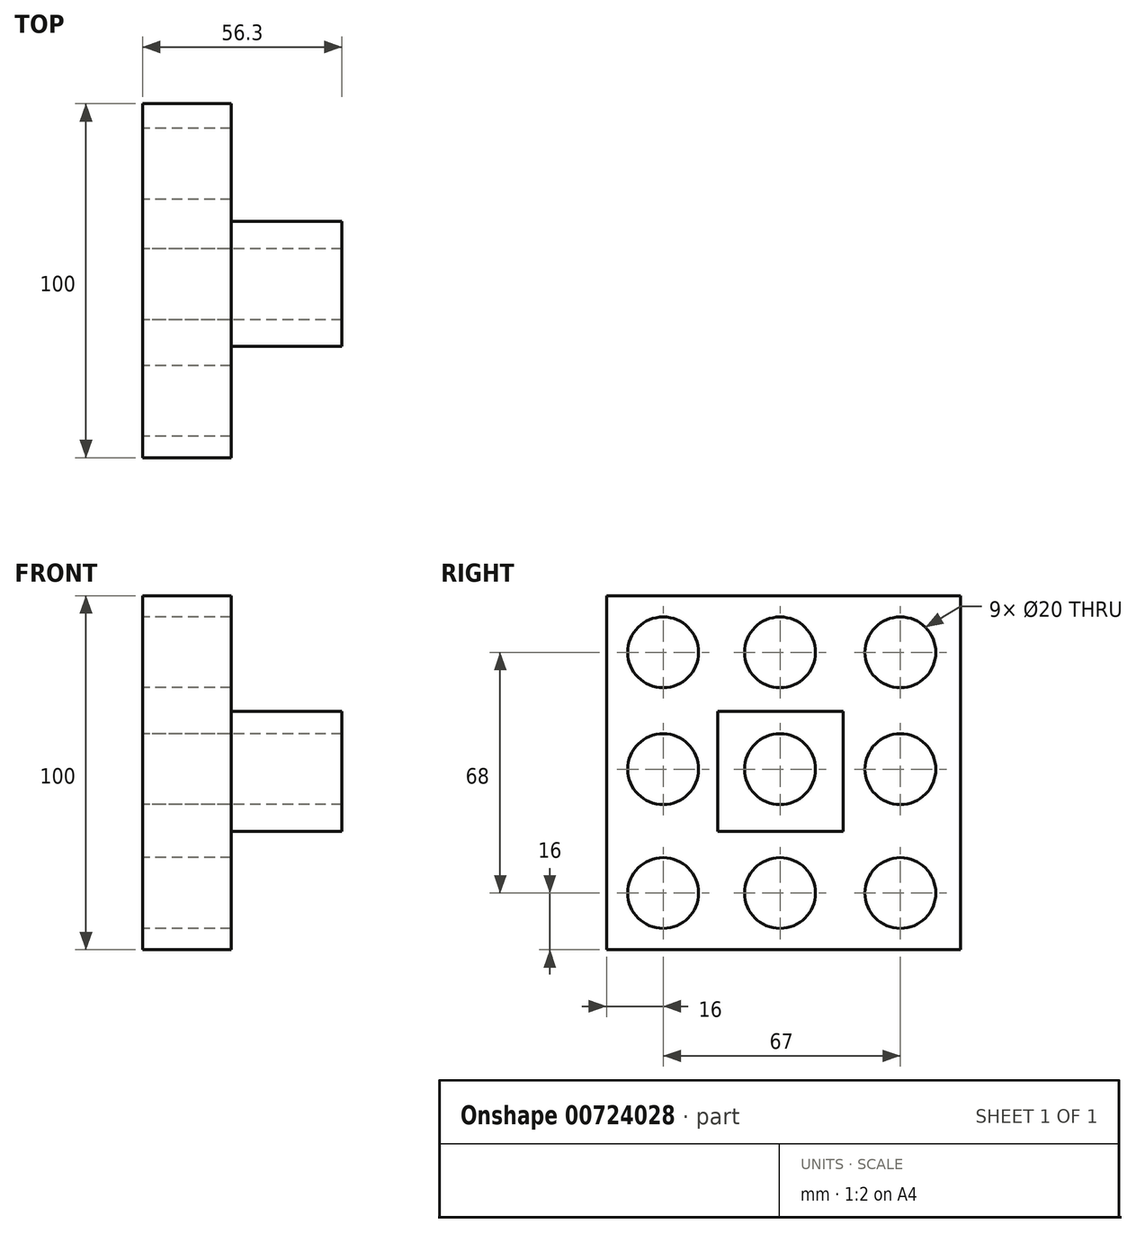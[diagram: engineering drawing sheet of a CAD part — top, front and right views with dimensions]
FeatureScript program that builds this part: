
annotation { "Feature Type Name" : "Feature", "Feature Type Description" : "" }
export const myFeature = defineFeature(function(context is Context, id is Id, definition is map)
    precondition{}
    {
        {
            var Q0;
            Q0=qCreatedBy(makeId("Right.planeOp"),FACE);
            var sketch = newSketch(context, id + "F0", { "sketchPlane" : qUnion([Q0])});
            skLineSegment(sketch, "E0.bottom", {"start": v(0, 0) * mm, "end": v(100, 0) * mm});
            skLineSegment(sketch, "E0.top", {"start": v(0, 100) * mm, "end": v(100, 100) * mm});
            skLineSegment(sketch, "E0.left", {"start": v(0, 0) * mm, "end": v(0, 100) * mm});
            skLineSegment(sketch, "E0.right", {"start": v(100, 0) * mm, "end": v(100, 100) * mm});
            skLineSegment(sketch, "E1.0", {"start": v(33, 0) * mm, "end": v(33, 100) * mm});
            skLineSegment(sketch, "E2.0", {"start": v(67, 0) * mm, "end": v(67, 100) * mm});
            skLineSegment(sketch, "E3.0", {"start": v(0, 67) * mm, "end": v(100, 67) * mm});
            skLineSegment(sketch, "E4.0", {"start": v(0, 33) * mm, "end": v(100, 33) * mm});
            skCircle(sketch, "E5", {"center": v(16, 16) * mm, "radius": 10 * mm});
            skCircle(sketch, "E6", {"center": v(49, 16) * mm, "radius": 10 * mm});
            skCircle(sketch, "E7", {"center": v(83, 16) * mm, "radius": 10 * mm});
            skCircle(sketch, "E8", {"center": v(16, 84) * mm, "radius": 10 * mm});
            skCircle(sketch, "E9", {"center": v(49, 84) * mm, "radius": 10 * mm});
            skPoint(sketch, "E9.centerSnap0", {"position": v(50, 84) * mm});
            skCircle(sketch, "E10", {"center": v(83, 84) * mm, "radius": 10 * mm});
            skCircle(sketch, "E11", {"center": v(16, 51) * mm, "radius": 10 * mm});
            skCircle(sketch, "E12", {"center": v(49, 51) * mm, "radius": 10 * mm});
            skCircle(sketch, "E13", {"center": v(83, 51) * mm, "radius": 10 * mm});
            skSolve(sketch);
        }
        {
            var Q0;
            Q0=makeQuery(id+"F0.imprint","IMPRINT",FACE,{"disambiguationData":[TD([[makeQuery(id+"F0.imprint","IMPRINT",EDGE,{"derivedFrom":sQuery(id+"F0.wireOp",EDGE,"E11")}),-1.0]])]});
            var Q1;
            Q1=makeQuery(id+"F0.imprint","IMPRINT",FACE,{"disambiguationData":[TD([[makeQuery(id+"F0.imprint","IMPRINT",EDGE,{"derivedFrom":sQuery(id+"F0.wireOp",EDGE,"E8")}),-1.0]])]});
            var Q2;
            Q2=makeQuery(id+"F0.imprint","IMPRINT",FACE,{"disambiguationData":[TD([[makeQuery(id+"F0.imprint","IMPRINT",EDGE,{"derivedFrom":sQuery(id+"F0.wireOp",EDGE,"E9")}),-1.0]])]});
            var Q3;
            Q3=makeQuery(id+"F0.imprint","IMPRINT",FACE,{"disambiguationData":[TD([[makeQuery(id+"F0.imprint","IMPRINT",EDGE,{"derivedFrom":sQuery(id+"F0.wireOp",EDGE,"E5")}),-1.0]])]});
            var Q4;
            Q4=makeQuery(id+"F0.imprint","IMPRINT",FACE,{"disambiguationData":[TD([[makeQuery(id+"F0.imprint","IMPRINT",EDGE,{"derivedFrom":sQuery(id+"F0.wireOp",EDGE,"E12")}),-1.0]])]});
            var Q5;
            Q5=makeQuery(id+"F0.imprint","IMPRINT",FACE,{"disambiguationData":[TD([[makeQuery(id+"F0.imprint","IMPRINT",EDGE,{"derivedFrom":sQuery(id+"F0.wireOp",EDGE,"E6")}),-1.0]])]});
            var Q6;
            Q6=makeQuery(id+"F0.imprint","IMPRINT",FACE,{"disambiguationData":[TD([[makeQuery(id+"F0.imprint","IMPRINT",EDGE,{"derivedFrom":sQuery(id+"F0.wireOp",EDGE,"E7")}),-1.0]])]});
            var Q7;
            Q7=makeQuery(id+"F0.imprint","IMPRINT",FACE,{"disambiguationData":[TD([[makeQuery(id+"F0.imprint","IMPRINT",EDGE,{"derivedFrom":sQuery(id+"F0.wireOp",EDGE,"E13")}),-1.0]])]});
            var Q8;
            Q8=makeQuery(id+"F0.imprint","IMPRINT",FACE,{"disambiguationData":[TD([[makeQuery(id+"F0.imprint","IMPRINT",EDGE,{"derivedFrom":sQuery(id+"F0.wireOp",EDGE,"E10")}),-1.0]])]});
            extrude(context, id + "F1", {"entities" : qUnion([Q0, Q1, Q2, Q3, Q4, Q5, Q6, Q7, Q8]), "depth" : 25 * mm, "offsetDistance" : 25 * mm});
        }
        {
            var Q0;
            Q0=qCreatedBy(makeId("Right.planeOp"),FACE);
            var sketch = newSketch(context, id + "F2", { "sketchPlane" : qUnion([Q0])});
            skLineSegment(sketch, "E14.0", {"start": v(0, 0) * mm, "end": v(0, 100) * mm});
            skLineSegment(sketch, "E15.0", {"start": v(0, 100) * mm, "end": v(100, 100) * mm});
            skLineSegment(sketch, "E16.0", {"start": v(100, 0) * mm, "end": v(100, 100) * mm});
            skLineSegment(sketch, "E17.0", {"start": v(0, 0) * mm, "end": v(100, 0) * mm});
            skLineSegment(sketch, "E18", {"start": v(31.53, 33.54) * mm, "end": v(66.7, 33.54) * mm});
            skLineSegment(sketch, "E19", {"start": v(31.43, 67.31) * mm, "end": v(66.8, 67.31) * mm});
            skLineSegment(sketch, "E20", {"start": v(31.53, 67.21) * mm, "end": v(31.53, 33.54) * mm});
            skLineSegment(sketch, "E21", {"start": v(66.8, 67.31) * mm, "end": v(66.8, 33.44) * mm});
            skLineSegment(sketch, "E22.0", {"start": v(31.43, 67.31) * mm, "end": v(31.43, 33.44) * mm});
            skLineSegment(sketch, "E23.0", {"start": v(66.7, 67.21) * mm, "end": v(66.7, 33.54) * mm});
            skLineSegment(sketch, "E24.0", {"start": v(31.53, 67.21) * mm, "end": v(66.7, 67.21) * mm});
            skLineSegment(sketch, "E25.0", {"start": v(31.43, 33.44) * mm, "end": v(66.8, 33.44) * mm});
            skPoint(sketch, "E26.orphan", {"position": v(66.8, 0) * mm});
            skPoint(sketch, "E27.trimOffspring.end.orphan", {"position": v(31.53, 0) * mm});
            skCircle(sketch, "E28.0", {"center": v(49, 51) * mm, "radius": 10 * mm});
            skSolve(sketch);
        }
        {
            var Q0;
            {var subQ0=sQuery(id+"F2.wireOp",EDGE,"E20");var subQ1=sQuery(id+"F2.wireOp",EDGE,"E19");var subQ2=makeQuery(id+"F2.imprint","INTERSECT",VERTEX,{"derivedFrom":[subQ1,subQ0]});Q0=makeQuery(id+"F2.imprint","IMPRINT",FACE,{"disambiguationData":[TD([[makeQuery(id+"F2.imprint","IMPRINT",EDGE,{"disambiguationData":[TD([[subQ2,-1.0]])],"derivedFrom":subQ1}),-1.0]])]});}
            var Q1;
            {var subQ0=sQuery(id+"F2.wireOp",EDGE,"E23.0");var subQ1=sQuery(id+"F2.wireOp",EDGE,"E18");var subQ2=makeQuery(id+"F2.imprint","INTERSECT",VERTEX,{"derivedFrom":[subQ1,subQ0]});Q1=makeQuery(id+"F2.imprint","IMPRINT",FACE,{"disambiguationData":[TD([[makeQuery(id+"F2.imprint","IMPRINT",EDGE,{"disambiguationData":[TD([[subQ2,-1.0]])],"derivedFrom":subQ1}),1.0]])]});}
            var Q2;
            {var subQ0=sQuery(id+"F2.wireOp",EDGE,"E20");var subQ1=sQuery(id+"F2.wireOp",EDGE,"E18");var subQ2=makeQuery(id+"F2.imprint","INTERSECT",VERTEX,{"derivedFrom":[subQ1,subQ0]});Q2=makeQuery(id+"F2.imprint","IMPRINT",FACE,{"disambiguationData":[TD([[makeQuery(id+"F2.imprint","IMPRINT",EDGE,{"disambiguationData":[TD([[subQ2,-1.0]])],"derivedFrom":subQ1}),-1.0]])]});}
            extrude(context, id + "F3", {"entities" : qUnion([Q0, Q1, Q2]), "operationType" : NewBodyOperationType.ADD, "depth" : 56.3 * mm, "offsetDistance" : 25 * mm});
        }
    });
